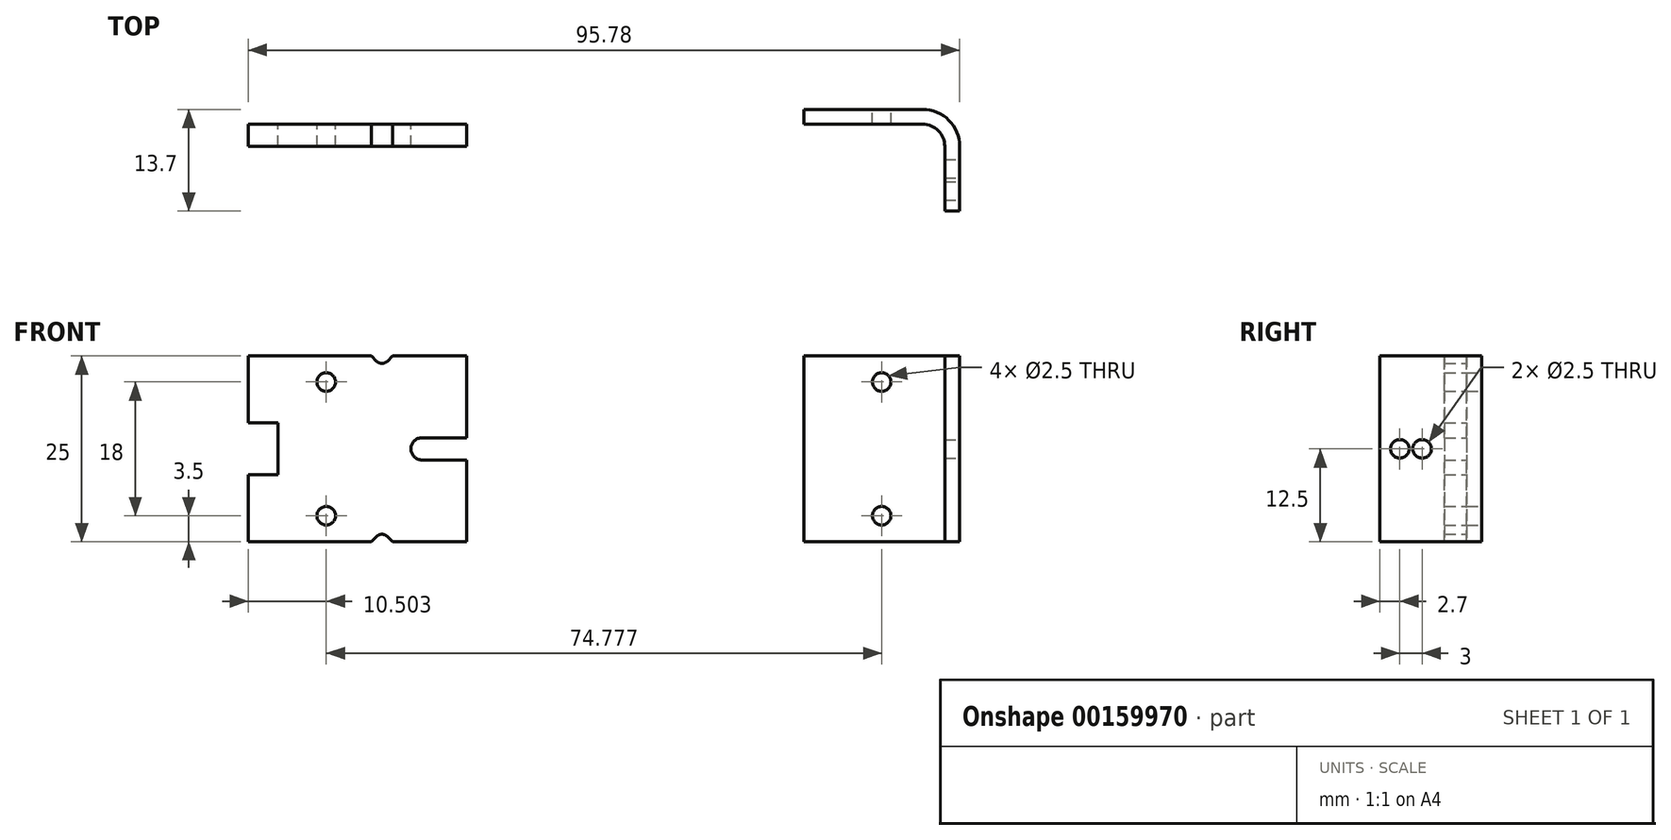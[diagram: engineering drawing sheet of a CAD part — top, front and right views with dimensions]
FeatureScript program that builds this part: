
annotation { "Feature Type Name" : "Feature", "Feature Type Description" : "" }
export const myFeature = defineFeature(function(context is Context, id is Id, definition is map)
    precondition{}
    {
        {
            var Q0;
            Q0=qCreatedBy(makeId("Top.planeOp"),FACE);
            var sketch = newSketch(context, id + "F0", { "sketchPlane" : qUnion([Q0])});
            skLineSegment(sketch, "E0.bottom", {"start": v(0, 0) * mm, "end": v(19, 0) * mm});
            skLineSegment(sketch, "E0.top", {"start": v(0, 2) * mm, "end": v(21, 2) * mm});
            skLineSegment(sketch, "E0.left", {"start": v(0, 0) * mm, "end": v(0, 2) * mm});
            skLineSegment(sketch, "E0.right", {"start": v(21, 0) * mm, "end": v(21, 2) * mm});
            skLineSegment(sketch, "E1.top", {"start": v(21, -11.7) * mm, "end": v(19, -11.7) * mm});
            skLineSegment(sketch, "E1.left", {"start": v(21, 0) * mm, "end": v(21, -11.7) * mm});
            skLineSegment(sketch, "E1.right", {"start": v(19, 0) * mm, "end": v(19, -11.7) * mm});
            skSolve(sketch);
        }
        {
            var Q0;
            Q0 = qSketchRegion(id + "F0", true);
            extrude(context, id + "F1", {"entities" : qUnion([Q0]), "depth" : 25 * mm});
        }
        {
            var Q0;
            Q0=makeQuery(id+"F1.opExtrude","SWEPT_EDGE",EDGE,{"disambiguationData":[OSD([sQuery(id+"F0.wireOp",EDGE,"E0.bottom"),sQuery(id+"F0.wireOp",EDGE,"E1.right")])]});
            fillet(context, id + "F2", {"entities" : qUnion([Q0]), "radius" : 3 * mm, "tangentPropagation" : true, "allowEdgeOverflow" : false});
        }
        {
            var Q0;
            Q0=makeQuery(id+"F1.opExtrude","SWEPT_FACE",FACE,{"disambiguationData":[OSD([sQuery(id+"F0.wireOp",EDGE,"E0.right"),sQuery(id+"F0.wireOp",EDGE,"E1.left")])]});
            var sketch = newSketch(context, id + "F3", { "sketchPlane" : qUnion([Q0])});
            skPoint(sketch, "E2.centerSnap0", {"position": v(-11.7, 12.5) * mm});
            skCircle(sketch, "E3.converted", {"center": v(-6, 12.5) * mm, "radius": 1.25 * mm});
            skCircle(sketch, "E4", {"center": v(-9, 12.5) * mm, "radius": 1.25 * mm});
            skLineSegment(sketch, "E5", {"start": v(-6, 12.5) * mm, "end": v(-9, 12.5) * mm, "construction": true});
            skSolve(sketch);
        }
        {
            var Q0;
            Q0 = qSketchRegion(id + "F3", true);
            extrude(context, id + "F4", {"entities" : qUnion([Q0]), "operationType" : NewBodyOperationType.REMOVE, "oppositeDirection" : true, "depth" : 25 * mm});
        }
        {
            var Q0;
            Q0=makeQuery(id+"F1.opExtrude","SWEPT_FACE",FACE,{"disambiguationData":[OSD([sQuery(id+"F0.wireOp",EDGE,"E0.top")])]});
            var sketch = newSketch(context, id + "F5", { "sketchPlane" : qUnion([Q0])});
            skCircle(sketch, "E6", {"center": v(-10.5, 21.5) * mm, "radius": 1.25 * mm});
            skPoint(sketch, "E6.centerSnap0", {"position": v(-10.5, 25) * mm});
            skCircle(sketch, "E7", {"center": v(-10.5, 3.5) * mm, "radius": 1.25 * mm});
            skLineSegment(sketch, "E8", {"start": v(-10.5, 3.5) * mm, "end": v(-10.5, 0) * mm, "construction": true});
            skLineSegment(sketch, "E9", {"start": v(-10.5, 21.5) * mm, "end": v(-10.5, 25) * mm, "construction": true});
            skSolve(sketch);
        }
        {
            var Q0;
            Q0 = qSketchRegion(id + "F5", true);
            extrude(context, id + "F6", {"entities" : qUnion([Q0]), "operationType" : NewBodyOperationType.REMOVE, "oppositeDirection" : true, "depth" : 25 * mm});
        }
        {
            var Q0;
            Q0=makeQuery(id+"F1.opExtrude","SWEPT_EDGE",EDGE,{"disambiguationData":[OSD([sQuery(id+"F0.wireOp",EDGE,"E0.top"),sQuery(id+"F0.wireOp",EDGE,"E0.right")])]});
            fillet(context, id + "F7", {"entities" : qUnion([Q0]), "radius" : 5 * mm, "tangentPropagation" : true, "allowEdgeOverflow" : false});
        }
        {
            var Q0;
            Q0=qCreatedBy(makeId("Front.planeOp"),FACE);
            var sketch = newSketch(context, id + "F8", { "sketchPlane" : qUnion([Q0])});
            skLineSegment(sketch, "E10.bottom", {"start": v(-74.78, 0) * mm, "end": v(-58.2, 0) * mm});
            skLineSegment(sketch, "E10.top", {"start": v(-74.78, 25) * mm, "end": v(-58.2, 25) * mm});
            skLineSegment(sketch, "E10.right", {"start": v(-45.36, 0) * mm, "end": v(-45.36, 11) * mm});
            skCircle(sketch, "E11", {"center": v(-64.28, 3.5) * mm, "radius": 1.25 * mm});
            skCircle(sketch, "E12", {"center": v(-64.28, 21.5) * mm, "radius": 1.25 * mm});
            skLineSegment(sketch, "E13", {"start": v(-64.28, 3.5) * mm, "end": v(-64.28, 21.5) * mm, "construction": true});
            skLineSegment(sketch, "E14", {"start": v(-64.28, 3.5) * mm, "end": v(-64.28, 0) * mm, "construction": true});
            skLineSegment(sketch, "E15", {"start": v(-64.28, 21.5) * mm, "end": v(-64.28, 25) * mm, "construction": true});
            skArc(sketch, "E16", {"start": v(-51.36, 14) * mm, "mid": v(-52.86, 12.5) * mm, "end": v(-51.36, 11) * mm});
            skLineSegment(sketch, "E17", {"start": v(-51.36, 12.5) * mm, "end": v(-51.06, 12.5) * mm, "construction": true});
            skLineSegment(sketch, "E18", {"start": v(-51.06, 12.5) * mm, "end": v(-51.06, 0) * mm, "construction": true});
            skLineSegment(sketch, "E19", {"start": v(-51.06, 12.5) * mm, "end": v(-51.06, 25) * mm, "construction": true});
            skLineSegment(sketch, "E20", {"start": v(-56.78, 0) * mm, "end": v(-56.78, 25) * mm, "construction": true});
            skLineSegment(sketch, "E21", {"start": v(-58.2, 0) * mm, "end": v(-57.48, 0.7) * mm});
            skLineSegment(sketch, "E22", {"start": v(-56.07, 0.7) * mm, "end": v(-55.36, 0) * mm});
            skLineSegment(sketch, "E23.trimOffspring", {"start": v(-55.36, 0) * mm, "end": v(-45.36, 0) * mm});
            skLineSegment(sketch, "E24", {"start": v(-56.07, 24.3) * mm, "end": v(-55.36, 25) * mm});
            skLineSegment(sketch, "E25", {"start": v(-57.48, 24.3) * mm, "end": v(-58.2, 25) * mm});
            skLineSegment(sketch, "E26.trimOffspring", {"start": v(-55.36, 25) * mm, "end": v(-45.36, 25) * mm});
            skPoint(sketch, "E27.visualSharp", {"position": v(-56.78, 23.59) * mm});
            skArc(sketch, "E27.filletArc", {"start": v(-57.48, 24.3) * mm, "mid": v(-56.78, 24) * mm, "end": v(-56.07, 24.3) * mm});
            skPoint(sketch, "E28.visualSharp", {"position": v(-56.78, 1.41) * mm});
            skArc(sketch, "E28.filletArc", {"start": v(-56.07, 0.7) * mm, "mid": v(-56.78, 1) * mm, "end": v(-57.48, 0.7) * mm});
            skLineSegment(sketch, "E29", {"start": v(-56.78, 1.41) * mm, "end": v(-56.78, 23.59) * mm});
            skLineSegment(sketch, "E30", {"start": v(-70.78, 16) * mm, "end": v(-70.78, 9) * mm});
            skLineSegment(sketch, "E31", {"start": v(-74.78, 25) * mm, "end": v(-74.78, 16) * mm});
            skLineSegment(sketch, "E32", {"start": v(-74.78, 16) * mm, "end": v(-70.78, 16) * mm});
            skLineSegment(sketch, "E33", {"start": v(-70.78, 9) * mm, "end": v(-74.78, 9) * mm});
            skLineSegment(sketch, "E34", {"start": v(-74.78, 9) * mm, "end": v(-74.78, 0) * mm});
            skLineSegment(sketch, "E35", {"start": v(-51.36, 14) * mm, "end": v(-45.36, 14) * mm});
            skLineSegment(sketch, "E36", {"start": v(-51.36, 11) * mm, "end": v(-45.36, 11) * mm});
            skLineSegment(sketch, "E37.trimOffspring", {"start": v(-45.36, 14) * mm, "end": v(-45.36, 25) * mm});
            skSolve(sketch);
        }
        {
            var Q0;
            Q0=makeQuery(id+"F8.imprint","IMPRINT",FACE,{"disambiguationData":[TD([[makeQuery(id+"F8.imprint","IMPRINT",EDGE,{"derivedFrom":sQuery(id+"F8.wireOp",EDGE,"E10.bottom")}),1.0]])]});
            extrude(context, id + "F9", {"entities" : qUnion([Q0]), "depth" : 3 * mm});
        }
    });
